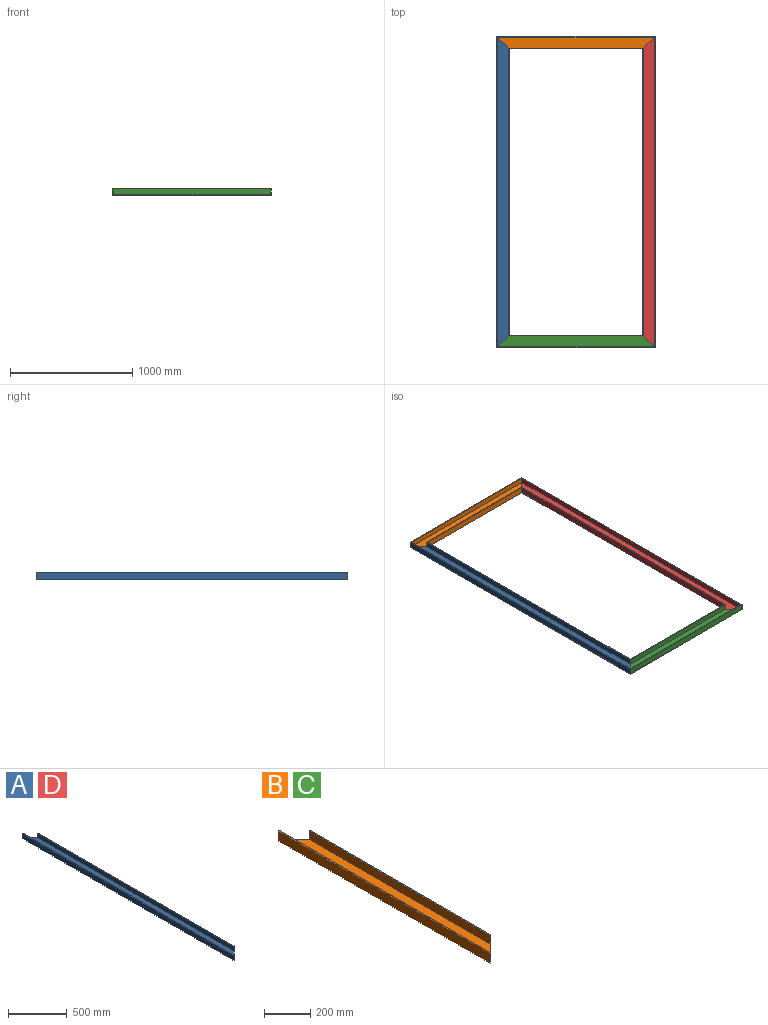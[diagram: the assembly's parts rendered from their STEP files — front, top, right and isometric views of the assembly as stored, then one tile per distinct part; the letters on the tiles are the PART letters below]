
ASSEMBLY  parts=4 mates=6
PART A: 10 faces, bbox 101.6x2543.2x50.8 mm
  f0: plane 2530.48x88.9mm, normal (0,0,1), area 217056mm2, adj f1,f3,f6,f8
  f1: plane 101.6x101.6mm, normal (0.71,-0.71,0), area 1710.7mm2, adj f0,f2,f4,f5,f6,f7,f8,f9
  f2: plane 2339.98x50.8mm, normal (1,0,0), area 118870.7mm2, adj f1,f3,f5,f7
  f3: plane 101.6x101.6mm, normal (0.71,0.71,0), area 1710.7mm2, adj f0,f2,f4,f5,f6,f7,f8,f9
  f4: plane 2543.18x50.8mm, normal (-1,0,0), area 129193.3mm2, adj f1,f3,f5,f9
  f5: plane 2543.18x101.6mm, normal (0,0,-1), area 248064mm2, adj f1,f2,f3,f4
  f6: plane 2352.68x44.45mm, normal (-1,0,0), area 104576.4mm2, adj f0,f1,f3,f7
  f7: plane 2352.68x6.35mm, normal (0,0,1), area 14899.2mm2, adj f1,f2,f3,f6
  f8: plane 2530.48x44.45mm, normal (1,0,0), area 112479.6mm2, adj f0,f1,f3,f9
  f9: plane 2543.18x6.35mm, normal (0,0,1), area 16108.8mm2, adj f1,f3,f4,f8
PART B: 10 faces, bbox 101.6x1293.8x50.8 mm
  f0: plane 1281.12x88.9mm, normal (0,0,1), area 105987.9mm2, adj f1,f3,f6,f8
  f1: plane 101.6x101.6mm, normal (0.71,-0.71,0), area 1710.7mm2, adj f0,f2,f4,f5,f6,f7,f8,f9
  f2: plane 1090.62x50.8mm, normal (1,0,0), area 55403.2mm2, adj f1,f3,f5,f7
  f3: plane 101.6x101.6mm, normal (0.71,0.71,0), area 1710.7mm2, adj f0,f2,f4,f5,f6,f7,f8,f9
  f4: plane 1293.82x50.8mm, normal (-1,0,0), area 65725.8mm2, adj f1,f3,f5,f9
  f5: plane 1293.82x101.6mm, normal (0,0,-1), area 121129mm2, adj f1,f2,f3,f4
  f6: plane 1103.32x44.45mm, normal (-1,0,0), area 49042.4mm2, adj f0,f1,f3,f7
  f7: plane 1103.32x6.35mm, normal (0,0,1), area 6965.7mm2, adj f1,f2,f3,f6
  f8: plane 1281.12x44.45mm, normal (1,0,0), area 56945.6mm2, adj f0,f1,f3,f9
  f9: plane 1293.82x6.35mm, normal (0,0,1), area 8175.4mm2, adj f1,f3,f4,f8
PART C: same geometry as B
PART D: same geometry as A
PLACE A t=(859.16,-105.29,67.06)mm
PLACE B rot(axis=(0,0,-1),90deg) t=(1455.27,1115.49,67.06)mm
PLACE C rot(axis=(0,0,1),90deg) t=(1455.27,-1326.08,67.06)mm
PLACE D rot(axis=(0,0,1),180deg) t=(2051.38,-105.29,67.06)mm
MATE planar B.f1 <-> A.f3  axis (-0.71,-0.71,0) through (859.16,1115.49,82.09)mm
MATE planar D.f3 <-> C.f1  axis (-0.71,-0.71,0) through (2051.38,-1326.08,82.09)mm
MATE planar B.f3 <-> D.f1  axis (0.71,-0.71,0) through (2051.38,1115.49,82.09)mm
MATE fastened C.f9 <-> A.f9  axis (0,0,1) through (808.36,-1376.88,117.86)mm
MATE planar D.f3 <-> C.f1  axis (-0.71,-0.71,0) through (2051.38,-1326.08,82.09)mm
MATE planar A.f0 <-> D.f0  axis (0,0,1) through (858.62,-105.29,73.41)mm
